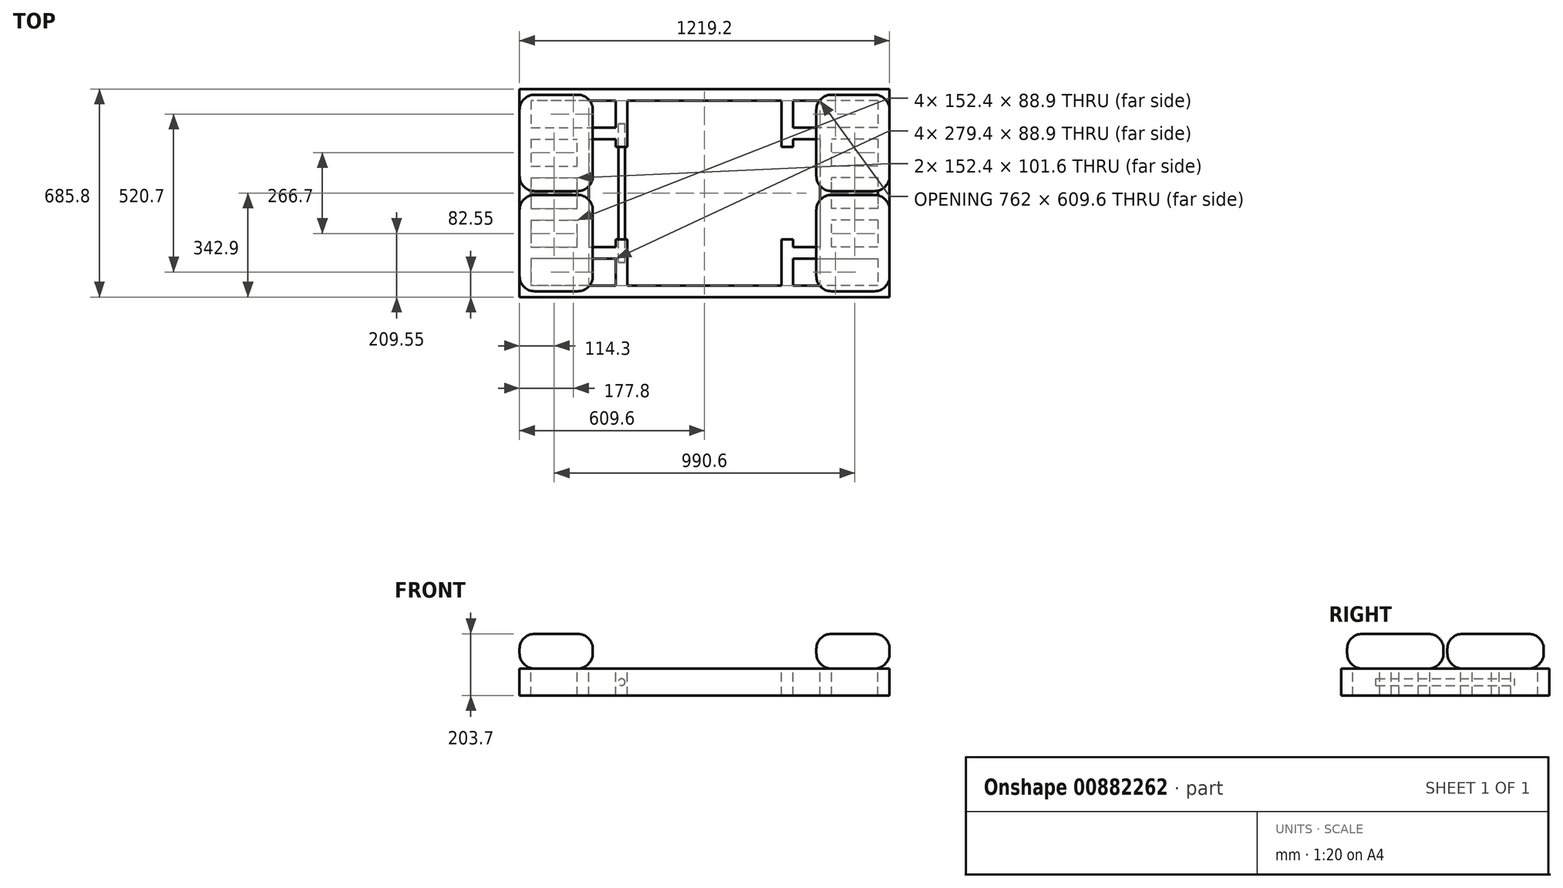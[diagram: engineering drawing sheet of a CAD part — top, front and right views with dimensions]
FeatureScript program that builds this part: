
annotation { "Feature Type Name" : "Feature", "Feature Type Description" : "" }
export const myFeature = defineFeature(function(context is Context, id is Id, definition is map)
    precondition{}
    {
        {
            var Q0;
            Q0=qCreatedBy(makeId("Top.planeOp"),FACE);
            var sketch = newSketch(context, id + "F0", { "sketchPlane" : qUnion([Q0])});
            skLineSegment(sketch, "E0.bottom", {"start": v(609.6, 342.9) * mm, "end": v(-609.6, 342.9) * mm});
            skLineSegment(sketch, "E0.top", {"start": v(609.6, -342.9) * mm, "end": v(-609.6, -342.9) * mm});
            skLineSegment(sketch, "E0.left", {"start": v(609.6, 342.9) * mm, "end": v(609.6, -342.9) * mm});
            skLineSegment(sketch, "E0.right", {"start": v(-609.6, 342.9) * mm, "end": v(-609.6, -342.9) * mm});
            skPoint(sketch, "E0.middle", {"position": v(0, 0) * mm});
            skLineSegment(sketch, "E1.0", {"start": v(571.5, 304.8) * mm, "end": v(-571.5, 304.8) * mm});
            skLineSegment(sketch, "E1.1", {"start": v(571.5, 304.8) * mm, "end": v(571.5, -304.8) * mm});
            skLineSegment(sketch, "E1.2", {"start": v(571.5, -304.8) * mm, "end": v(-571.5, -304.8) * mm});
            skLineSegment(sketch, "E1.3", {"start": v(-571.5, 304.8) * mm, "end": v(-571.5, -304.8) * mm});
            skLineSegment(sketch, "E2", {"start": v(-571.5, 215.9) * mm, "end": v(-292.1, 215.9) * mm});
            skLineSegment(sketch, "E3", {"start": v(-571.5, 177.8) * mm, "end": v(-292.1, 177.8) * mm});
            skLineSegment(sketch, "E4", {"start": v(-571.5, 88.9) * mm, "end": v(-419.1, 88.9) * mm});
            skLineSegment(sketch, "E5", {"start": v(-571.5, 50.8) * mm, "end": v(-419.1, 50.8) * mm});
            skLineSegment(sketch, "E6", {"start": v(-571.5, -50.8) * mm, "end": v(-419.1, -50.8) * mm});
            skLineSegment(sketch, "E7", {"start": v(-571.5, -88.9) * mm, "end": v(-419.1, -88.9) * mm});
            skLineSegment(sketch, "E8", {"start": v(-571.5, -177.8) * mm, "end": v(-292.1, -177.8) * mm});
            skLineSegment(sketch, "E9", {"start": v(-292.1, -215.9) * mm, "end": v(-571.5, -215.9) * mm});
            skLineSegment(sketch, "E10", {"start": v(0, 202.96) * mm, "end": v(0, -200.88) * mm, "construction": true});
            skLineSegment(sketch, "E11.MirrorCS", {"start": v(571.5, 215.9) * mm, "end": v(292.1, 215.9) * mm});
            skLineSegment(sketch, "E12.MirrorCS", {"start": v(571.5, 177.8) * mm, "end": v(292.1, 177.8) * mm});
            skLineSegment(sketch, "E13.MirrorCS", {"start": v(571.5, 50.8) * mm, "end": v(419.1, 50.8) * mm});
            skLineSegment(sketch, "E14.MirrorCS", {"start": v(571.5, 88.9) * mm, "end": v(419.1, 88.9) * mm});
            skLineSegment(sketch, "E15.MirrorCS", {"start": v(571.5, -50.8) * mm, "end": v(419.1, -50.8) * mm});
            skLineSegment(sketch, "E16.MirrorCS", {"start": v(571.5, -88.9) * mm, "end": v(419.1, -88.9) * mm});
            skLineSegment(sketch, "E17.MirrorCS", {"start": v(571.5, -177.8) * mm, "end": v(292.1, -177.8) * mm});
            skLineSegment(sketch, "E18.MirrorCS", {"start": v(292.1, -215.9) * mm, "end": v(571.5, -215.9) * mm});
            skLineSegment(sketch, "E19", {"start": v(-292.1, 304.8) * mm, "end": v(-292.1, 152.4) * mm});
            skLineSegment(sketch, "E20", {"start": v(-292.1, 152.4) * mm, "end": v(-254, 152.4) * mm});
            skLineSegment(sketch, "E21", {"start": v(-254, 152.4) * mm, "end": v(-254, 304.8) * mm});
            skLineSegment(sketch, "E22", {"start": v(-105.83, 0) * mm, "end": v(131.55, 0) * mm, "construction": true});
            skLineSegment(sketch, "E23.MirrorCS", {"start": v(-292.1, -152.4) * mm, "end": v(-254, -152.4) * mm});
            skLineSegment(sketch, "E24.MirrorCS", {"start": v(-292.1, -304.8) * mm, "end": v(-292.1, -152.4) * mm});
            skLineSegment(sketch, "E25.MirrorCS", {"start": v(-254, -152.4) * mm, "end": v(-254, -304.8) * mm});
            skLineSegment(sketch, "E26.MirrorCS", {"start": v(292.1, 304.8) * mm, "end": v(292.1, 152.4) * mm});
            skLineSegment(sketch, "E27.MirrorCS", {"start": v(254, 152.4) * mm, "end": v(254, 304.8) * mm});
            skLineSegment(sketch, "E28.MirrorCS", {"start": v(254, -152.4) * mm, "end": v(254, -304.8) * mm});
            skLineSegment(sketch, "E29.MirrorCS", {"start": v(292.1, -304.8) * mm, "end": v(292.1, -152.4) * mm});
            skLineSegment(sketch, "E30.MirrorCS", {"start": v(292.1, -152.4) * mm, "end": v(254, -152.4) * mm});
            skLineSegment(sketch, "E31.MirrorCS", {"start": v(292.1, 152.4) * mm, "end": v(254, 152.4) * mm});
            skLineSegment(sketch, "E32", {"start": v(-381, 177.8) * mm, "end": v(-381, -177.8) * mm});
            skLineSegment(sketch, "E33", {"start": v(-419.1, -177.8) * mm, "end": v(-419.1, 177.8) * mm});
            skLineSegment(sketch, "E34.MirrorCS", {"start": v(381, 177.8) * mm, "end": v(381, -177.8) * mm});
            skLineSegment(sketch, "E35.MirrorCS", {"start": v(419.1, -177.8) * mm, "end": v(419.1, 177.8) * mm});
            skSolve(sketch);
        }
        {
            var Q0;
            Q0 = qSketchRegion(id + "F0", true);
            var Q1;
            {var subQ0=sQuery(id+"F0.wireOp",EDGE,"E8");Q1=makeQuery(id+"F0.imprint","IMPRINT",FACE,{"disambiguationData":[TD([[makeQuery(id+"F0.imprint","IMPRINT",EDGE,{"derivedFrom":subQ0}),-1.0]])]});}
            var Q2;
            {var subQ0=sQuery(id+"F0.wireOp",EDGE,"E6");Q2=makeQuery(id+"F0.imprint","IMPRINT",FACE,{"disambiguationData":[TD([[makeQuery(id+"F0.imprint","IMPRINT",EDGE,{"derivedFrom":subQ0}),-1.0]])]});}
            var Q3;
            {var subQ0=sQuery(id+"F0.wireOp",EDGE,"E4");Q3=makeQuery(id+"F0.imprint","IMPRINT",FACE,{"disambiguationData":[TD([[makeQuery(id+"F0.imprint","IMPRINT",EDGE,{"derivedFrom":subQ0}),-1.0]])]});}
            var Q4;
            {var subQ0=sQuery(id+"F0.wireOp",EDGE,"E2");Q4=makeQuery(id+"F0.imprint","IMPRINT",FACE,{"disambiguationData":[TD([[makeQuery(id+"F0.imprint","IMPRINT",EDGE,{"derivedFrom":subQ0}),-1.0]])]});}
            var Q5;
            {var subQ7=sQuery(id+"F0.wireOp",EDGE,"cwWb0SoG-ZnSS-VYmK-vyH5-mZEmu31jRke6");Q5=makeQuery(id+"F0.imprint","IMPRINT",FACE,{"disambiguationData":[TD([[makeQuery(id+"F0.imprint","IMPRINT",EDGE,{"derivedFrom":subQ7}),-1.0]])]});}
            var Q6;
            {var subQ10=sQuery(id+"F0.wireOp",EDGE,"99df57b3-d25c-4799-a7b8-9894685af46e.0");Q6=makeQuery(id+"F0.imprint","IMPRINT",FACE,{"disambiguationData":[TD([[makeQuery(id+"F0.imprint","IMPRINT",EDGE,{"derivedFrom":subQ10}),1.0]])]});}
            var Q7;
            {var subQ0=sQuery(id+"F0.wireOp",EDGE,"E11.MirrorCS");Q7=makeQuery(id+"F0.imprint","IMPRINT",FACE,{"disambiguationData":[TD([[makeQuery(id+"F0.imprint","IMPRINT",EDGE,{"derivedFrom":subQ0}),1.0]])]});}
            var Q8;
            {var subQ0=sQuery(id+"F0.wireOp",EDGE,"E13.MirrorCS");Q8=makeQuery(id+"F0.imprint","IMPRINT",FACE,{"disambiguationData":[TD([[makeQuery(id+"F0.imprint","IMPRINT",EDGE,{"derivedFrom":subQ0}),-1.0]])]});}
            var Q9;
            {var subQ0=sQuery(id+"F0.wireOp",EDGE,"E15.MirrorCS");Q9=makeQuery(id+"F0.imprint","IMPRINT",FACE,{"disambiguationData":[TD([[makeQuery(id+"F0.imprint","IMPRINT",EDGE,{"derivedFrom":subQ0}),1.0]])]});}
            var Q10;
            {var subQ0=sQuery(id+"F0.wireOp",EDGE,"E17.MirrorCS");Q10=makeQuery(id+"F0.imprint","IMPRINT",FACE,{"disambiguationData":[TD([[makeQuery(id+"F0.imprint","IMPRINT",EDGE,{"derivedFrom":subQ0}),1.0]])]});}
            var Q11;
            {var subQ4=sQuery(id+"F0.wireOp",EDGE,"E32");Q11=makeQuery(id+"F0.imprint","IMPRINT",FACE,{"disambiguationData":[TD([[makeQuery(id+"F0.imprint","IMPRINT",EDGE,{"derivedFrom":subQ4}),-1.0]])]});}
            var Q12;
            {var subQ2=sQuery(id+"F0.wireOp",EDGE,"E20");Q12=makeQuery(id+"F0.imprint","IMPRINT",FACE,{"disambiguationData":[TD([[makeQuery(id+"F0.imprint","IMPRINT",EDGE,{"derivedFrom":subQ2}),1.0]])]});}
            var Q13;
            {var subQ5=sQuery(id+"F0.wireOp",EDGE,"E23.MirrorCS");Q13=makeQuery(id+"F0.imprint","IMPRINT",FACE,{"disambiguationData":[TD([[makeQuery(id+"F0.imprint","IMPRINT",EDGE,{"derivedFrom":subQ5}),-1.0]])]});}
            var Q14;
            {var subQ5=sQuery(id+"F0.wireOp",EDGE,"E28.MirrorCS");Q14=makeQuery(id+"F0.imprint","IMPRINT",FACE,{"disambiguationData":[TD([[makeQuery(id+"F0.imprint","IMPRINT",EDGE,{"derivedFrom":subQ5}),1.0]])]});}
            var Q15;
            {var subQ6=sQuery(id+"F0.wireOp",EDGE,"E27.MirrorCS");Q15=makeQuery(id+"F0.imprint","IMPRINT",FACE,{"disambiguationData":[TD([[makeQuery(id+"F0.imprint","IMPRINT",EDGE,{"derivedFrom":subQ6}),-1.0]])]});}
            var Q16;
            {var subQ0=sQuery(id+"F0.wireOp",EDGE,"E34.MirrorCS");Q16=makeQuery(id+"F0.imprint","IMPRINT",FACE,{"disambiguationData":[TD([[makeQuery(id+"F0.imprint","IMPRINT",EDGE,{"derivedFrom":subQ0}),1.0]])]});}
            extrude(context, id + "F1", {"entities" : qUnion([Q0, Q1, Q2, Q3, Q4, Q5, Q6, Q7, Q8, Q9, Q10, Q11, Q12, Q13, Q14, Q15, Q16]), "endBound" : BoundingType.SYMMETRIC, "oppositeDirection" : true, "depth" : 88.9 * mm, "offsetDistance" : 25 * mm});
        }
        {
            var Q0;
            Q0=makeQuery(id+"F1.opExtrude","CAP_FACE",FACE,{"disambiguationData":[OSD([sQuery(id+"F0.wireOp",EDGE,"E0.bottom"),sQuery(id+"F0.wireOp",EDGE,"E0.top"),sQuery(id+"F0.wireOp",EDGE,"E0.left"),sQuery(id+"F0.wireOp",EDGE,"E0.right"),sQuery(id+"F0.wireOp",EDGE,"E1.0"),sQuery(id+"F0.wireOp",EDGE,"E1.1"),sQuery(id+"F0.wireOp",EDGE,"E1.2"),sQuery(id+"F0.wireOp",EDGE,"E1.3"),sQuery(id+"F0.wireOp",EDGE,"cwWb0SoG-ZnSS-VYmK-vyH5-mZEmu31jRke6"),sQuery(id+"F0.wireOp",EDGE,"VBJxguFo-qtos-i8gi-4R7U-pl60S83nKZb7"),sQuery(id+"F0.wireOp",EDGE,"0b26652e-e3b5-4e32-8bd5-1aea19a4eb36.0"),sQuery(id+"F0.wireOp",EDGE,"99df57b3-d25c-4799-a7b8-9894685af46e.0"),sQuery(id+"F0.wireOp",EDGE,"E2"),sQuery(id+"F0.wireOp",EDGE,"E3"),sQuery(id+"F0.wireOp",EDGE,"E4"),sQuery(id+"F0.wireOp",EDGE,"E5"),sQuery(id+"F0.wireOp",EDGE,"E6"),sQuery(id+"F0.wireOp",EDGE,"E7"),sQuery(id+"F0.wireOp",EDGE,"E8"),sQuery(id+"F0.wireOp",EDGE,"E9"),sQuery(id+"F0.wireOp",EDGE,"E11.MirrorCS"),sQuery(id+"F0.wireOp",EDGE,"E12.MirrorCS"),sQuery(id+"F0.wireOp",EDGE,"E13.MirrorCS"),sQuery(id+"F0.wireOp",EDGE,"E14.MirrorCS"),sQuery(id+"F0.wireOp",EDGE,"E15.MirrorCS"),sQuery(id+"F0.wireOp",EDGE,"E16.MirrorCS"),sQuery(id+"F0.wireOp",EDGE,"E17.MirrorCS"),sQuery(id+"F0.wireOp",EDGE,"E18.MirrorCS")])],"isStart":true});
            cPlane(context, id + "F2", {"entities" : qUnion([Q0]), "cplaneType" : CPlaneType.OFFSET, "offset" : .5 * mm, "width" : 150 * mm, "height" : 150 * mm});
        }
        {
            var Q0;
            Q0=qCreatedBy(id+"F2.planeOp",FACE);
            var sketch = newSketch(context, id + "F3", { "sketchPlane" : qUnion([Q0])});
            skLineSegment(sketch, "E36.bottom", {"start": v(609.6, 323.85) * mm, "end": v(368.3, 323.85) * mm});
            skLineSegment(sketch, "E36.top", {"start": v(609.6, 6.35) * mm, "end": v(368.3, 6.35) * mm});
            skLineSegment(sketch, "E36.left", {"start": v(609.6, 323.85) * mm, "end": v(609.6, 6.35) * mm});
            skLineSegment(sketch, "E36.right", {"start": v(368.3, 323.85) * mm, "end": v(368.3, 6.35) * mm});
            skPoint(sketch, "E36.middle", {"position": v(488.95, 165.1) * mm});
            skLineSegment(sketch, "E37.bottom", {"start": v(609.6, -6.35) * mm, "end": v(368.3, -6.35) * mm});
            skLineSegment(sketch, "E37.top", {"start": v(609.6, -323.85) * mm, "end": v(368.3, -323.85) * mm});
            skLineSegment(sketch, "E37.left", {"start": v(609.6, -6.35) * mm, "end": v(609.6, -323.85) * mm});
            skLineSegment(sketch, "E37.right", {"start": v(368.3, -6.35) * mm, "end": v(368.3, -323.85) * mm});
            skPoint(sketch, "E37.middle", {"position": v(488.95, -165.1) * mm});
            skPoint(sketch, "E37.centerSnap0", {"position": v(488.95, 6.35) * mm});
            skLineSegment(sketch, "E38", {"start": v(0, 196.25) * mm, "end": v(0, -204.18) * mm, "construction": true});
            skLineSegment(sketch, "E39.MirrorCS", {"start": v(-609.6, -323.85) * mm, "end": v(-368.3, -323.85) * mm});
            skLineSegment(sketch, "E40.MirrorCS", {"start": v(-609.6, 323.85) * mm, "end": v(-609.6, 6.35) * mm});
            skPoint(sketch, "E41.MirrorP", {"position": v(-488.95, 6.35) * mm});
            skPoint(sketch, "E42.MirrorP", {"position": v(-488.95, -165.1) * mm});
            skLineSegment(sketch, "E43.MirrorCS", {"start": v(-609.6, 6.35) * mm, "end": v(-368.3, 6.35) * mm});
            skLineSegment(sketch, "E44.MirrorCS", {"start": v(-609.6, -6.35) * mm, "end": v(-368.3, -6.35) * mm});
            skLineSegment(sketch, "E45.MirrorCS", {"start": v(-368.3, 323.85) * mm, "end": v(-368.3, 6.35) * mm});
            skLineSegment(sketch, "E46.MirrorCS", {"start": v(-609.6, -6.35) * mm, "end": v(-609.6, -323.85) * mm});
            skLineSegment(sketch, "E47.MirrorCS", {"start": v(-368.3, -6.35) * mm, "end": v(-368.3, -323.85) * mm});
            skLineSegment(sketch, "E48.MirrorCS", {"start": v(-609.6, 323.85) * mm, "end": v(-368.3, 323.85) * mm});
            skPoint(sketch, "E49.MirrorP", {"position": v(-488.95, 165.1) * mm});
            skSolve(sketch);
        }
        {
            var Q0;
            Q0 = qSketchRegion(id + "F3", true);
            extrude(context, id + "F4", {"entities" : qUnion([Q0]), "depth" : 114.3 * mm, "offsetDistance" : 25 * mm});
        }
        {
            var Q0;
            Q0=makeQuery(id+"F4.opExtrude","CAP_FACE",FACE,{"disambiguationData":[OSD([sQuery(id+"F3.wireOp",EDGE,"E40.MirrorCS"),sQuery(id+"F3.wireOp",EDGE,"E43.MirrorCS"),sQuery(id+"F3.wireOp",EDGE,"E45.MirrorCS"),sQuery(id+"F3.wireOp",EDGE,"E48.MirrorCS")])],"isStart":false});
            var Q1;
            Q1=makeQuery(id+"F4.opExtrude","CAP_FACE",FACE,{"disambiguationData":[OSD([sQuery(id+"F3.wireOp",EDGE,"E39.MirrorCS"),sQuery(id+"F3.wireOp",EDGE,"E44.MirrorCS"),sQuery(id+"F3.wireOp",EDGE,"E46.MirrorCS"),sQuery(id+"F3.wireOp",EDGE,"E47.MirrorCS")])],"isStart":false});
            var Q2;
            Q2=makeQuery(id+"F4.opExtrude","CAP_FACE",FACE,{"disambiguationData":[OSD([sQuery(id+"F3.wireOp",EDGE,"E37.bottom"),sQuery(id+"F3.wireOp",EDGE,"E37.top"),sQuery(id+"F3.wireOp",EDGE,"E37.left"),sQuery(id+"F3.wireOp",EDGE,"E37.right")])],"isStart":false});
            var Q3;
            Q3=makeQuery(id+"F4.opExtrude","CAP_FACE",FACE,{"disambiguationData":[OSD([sQuery(id+"F3.wireOp",EDGE,"E36.bottom"),sQuery(id+"F3.wireOp",EDGE,"E36.top"),sQuery(id+"F3.wireOp",EDGE,"E36.left"),sQuery(id+"F3.wireOp",EDGE,"E36.right")])],"isStart":false});
            var Q4;
            Q4=makeQuery(id+"F4.opExtrude","SWEPT_FACE",FACE,{"disambiguationData":[OSD([sQuery(id+"F3.wireOp",EDGE,"E46.MirrorCS")])]});
            var Q5;
            Q5=makeQuery(id+"F4.opExtrude","SWEPT_FACE",FACE,{"disambiguationData":[OSD([sQuery(id+"F3.wireOp",EDGE,"E40.MirrorCS")])]});
            var Q6;
            Q6=makeQuery(id+"F4.opExtrude","SWEPT_FACE",FACE,{"disambiguationData":[OSD([sQuery(id+"F3.wireOp",EDGE,"E36.right")])]});
            var Q7;
            Q7=makeQuery(id+"F4.opExtrude","SWEPT_FACE",FACE,{"disambiguationData":[OSD([sQuery(id+"F3.wireOp",EDGE,"E37.right")])]});
            var Q8;
            Q8=makeQuery(id+"F4.opExtrude","SWEPT_FACE",FACE,{"disambiguationData":[OSD([sQuery(id+"F3.wireOp",EDGE,"E47.MirrorCS")])]});
            var Q9;
            Q9=makeQuery(id+"F4.opExtrude","CAP_EDGE",EDGE,{"disambiguationData":[OSD([sQuery(id+"F3.wireOp",EDGE,"E45.MirrorCS")])],"isStart":true});
            var Q10;
            Q10=makeQuery(id+"F4.opExtrude","SWEPT_FACE",FACE,{"disambiguationData":[OSD([sQuery(id+"F3.wireOp",EDGE,"E36.left")])]});
            var Q11;
            Q11=makeQuery(id+"F4.opExtrude","SWEPT_FACE",FACE,{"disambiguationData":[OSD([sQuery(id+"F3.wireOp",EDGE,"E37.left")])]});
            var Q12;
            Q12=makeQuery(id+"F4.opExtrude","CAP_FACE",FACE,{"disambiguationData":[OSD([sQuery(id+"F3.wireOp",EDGE,"E36.bottom"),sQuery(id+"F3.wireOp",EDGE,"E36.top"),sQuery(id+"F3.wireOp",EDGE,"E36.left"),sQuery(id+"F3.wireOp",EDGE,"E36.right")])],"isStart":true});
            var Q13;
            Q13=makeQuery(id+"F4.opExtrude","CAP_FACE",FACE,{"disambiguationData":[OSD([sQuery(id+"F3.wireOp",EDGE,"E40.MirrorCS"),sQuery(id+"F3.wireOp",EDGE,"E43.MirrorCS"),sQuery(id+"F3.wireOp",EDGE,"E45.MirrorCS"),sQuery(id+"F3.wireOp",EDGE,"E48.MirrorCS")])],"isStart":true});
            var Q14;
            Q14=makeQuery(id+"F4.opExtrude","CAP_FACE",FACE,{"disambiguationData":[OSD([sQuery(id+"F3.wireOp",EDGE,"E39.MirrorCS"),sQuery(id+"F3.wireOp",EDGE,"E44.MirrorCS"),sQuery(id+"F3.wireOp",EDGE,"E46.MirrorCS"),sQuery(id+"F3.wireOp",EDGE,"E47.MirrorCS")])],"isStart":true});
            var Q15;
            Q15=makeQuery(id+"F4.opExtrude","SWEPT_FACE",FACE,{"disambiguationData":[OSD([sQuery(id+"F3.wireOp",EDGE,"E45.MirrorCS")])]});
            var Q16;
            Q16=makeQuery(id+"F4.opExtrude","CAP_FACE",FACE,{"disambiguationData":[OSD([sQuery(id+"F3.wireOp",EDGE,"E37.bottom"),sQuery(id+"F3.wireOp",EDGE,"E37.top"),sQuery(id+"F3.wireOp",EDGE,"E37.left"),sQuery(id+"F3.wireOp",EDGE,"E37.right")])],"isStart":true});
            fillet(context, id + "F5", {"entities" : qUnion([Q0, Q1, Q2, Q3, Q4, Q5, Q6, Q7, Q8, Q9, Q10, Q11, Q12, Q13, Q14, Q15, Q16]), "radius" : 50 * mm, "tangentPropagation" : true, "allowEdgeOverflow" : false});
        }
        {
            var Q0;
            Q0=qCreatedBy(makeId("Front.planeOp"),FACE);
            var sketch = newSketch(context, id + "F6", { "sketchPlane" : qUnion([Q0])});
            skCircle(sketch, "E50", {"center": v(-273.05, 0) * mm, "radius": 11.05 * mm});
            skLineSegment(sketch, "E51", {"start": v(0, 36.86) * mm, "end": v(0, -50.65) * mm, "construction": true});
            skCircle(sketch, "E52.MirrorC", {"center": v(273.05, 0) * mm, "radius": 11.05 * mm});
            skSolve(sketch);
        }
        {
            var Q0;
            Q0=makeQuery(id+"F6.imprint","IMPRINT",FACE,{"disambiguationData":[TD([[makeQuery(id+"F6.imprint","IMPRINT",EDGE,{"derivedFrom":sQuery(id+"F6.wireOp",EDGE,"E50")}),1.0]])]});
            var Q1;
            Q1=makeQuery(id+"F6.imprint","IMPRINT",FACE,{"disambiguationData":[TD([[makeQuery(id+"F6.imprint","IMPRINT",EDGE,{"derivedFrom":sQuery(id+"F6.wireOp",EDGE,"E52.MirrorC")}),-1.0]])]});
            extrude(context, id + "F7", {"entities" : qUnion([Q0, Q1]), "endBound" : BoundingType.SYMMETRIC, "depth" : 457.2 * mm, "offsetDistance" : 25.4 * mm});
        }
    });
